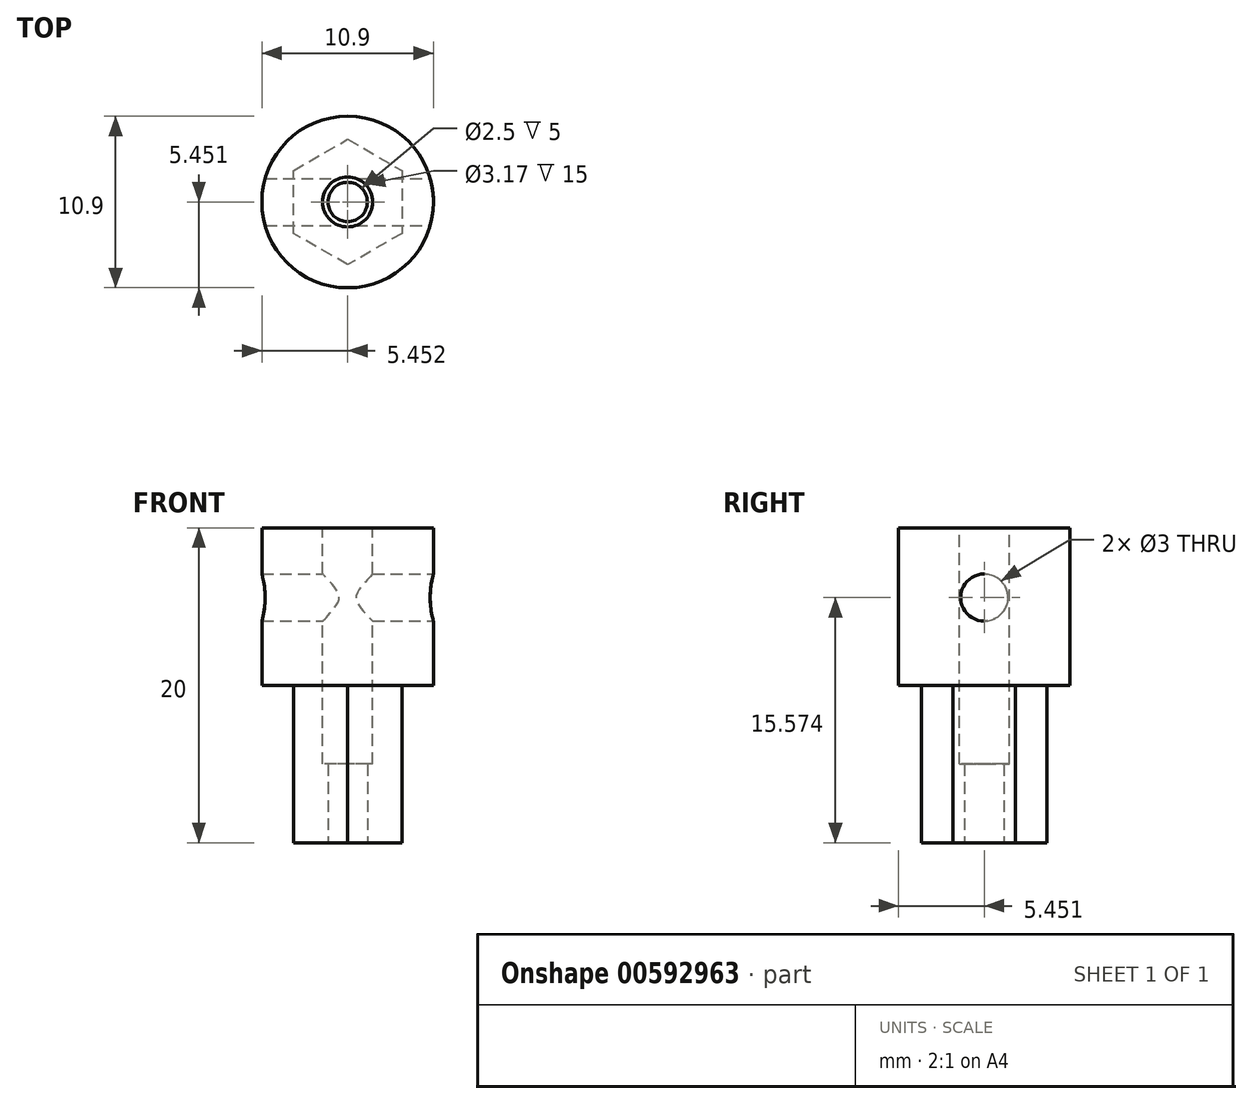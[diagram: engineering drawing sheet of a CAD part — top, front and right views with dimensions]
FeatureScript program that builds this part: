
annotation { "Feature Type Name" : "Feature", "Feature Type Description" : "" }
export const myFeature = defineFeature(function(context is Context, id is Id, definition is map)
    precondition{}
    {
        {
            var Q0;
            Q0=qCreatedBy(makeId("Top.planeOp"),FACE);
            var sketch = newSketch(context, id + "F0", { "sketchPlane" : qUnion([Q0])});
            skCircle(sketch, "E0.cCircle", {"center": v(2.23, 0.88) * mm, "radius": 3.98 * mm, "construction": true});
            skLineSegment(sketch, "E0.0", {"start": v(5.68, -1.11) * mm, "end": v(2.23, -3.1) * mm});
            skLineSegment(sketch, "E0.1", {"start": v(2.23, -3.1) * mm, "end": v(-1.22, -1.11) * mm});
            skLineSegment(sketch, "E0.2", {"start": v(-1.22, -1.11) * mm, "end": v(-1.22, 2.87) * mm});
            skLineSegment(sketch, "E0.3", {"start": v(-1.22, 2.87) * mm, "end": v(2.23, 4.86) * mm});
            skLineSegment(sketch, "E0.4", {"start": v(2.23, 4.86) * mm, "end": v(5.68, 2.87) * mm});
            skLineSegment(sketch, "E0.5", {"start": v(5.68, 2.87) * mm, "end": v(5.68, -1.11) * mm});
            skCircle(sketch, "E1", {"center": v(2.23, 0.88) * mm, "radius": 1.25 * mm});
            skSolve(sketch);
        }
        {
            var Q0;
            Q0=makeQuery(id+"F0.imprint","IMPRINT",FACE,{"disambiguationData":[TD([[makeQuery(id+"F0.imprint","IMPRINT",EDGE,{"derivedFrom":sQuery(id+"F0.wireOp",EDGE,"E0.0")}),-1.0]])]});
            extrude(context, id + "F1", {"entities" : qUnion([Q0]), "depth" : 10 * mm, "offsetDistance" : 25 * mm});
        }
        {
            var Q0;
            Q0=makeQuery(id+"F1.opExtrude","CAP_FACE",FACE,{"disambiguationData":[OSD([sQuery(id+"F0.wireOp",EDGE,"E0.0"),sQuery(id+"F0.wireOp",EDGE,"E0.1"),sQuery(id+"F0.wireOp",EDGE,"E0.2"),sQuery(id+"F0.wireOp",EDGE,"E0.3"),sQuery(id+"F0.wireOp",EDGE,"E0.4"),sQuery(id+"F0.wireOp",EDGE,"E0.5"),sQuery(id+"F0.wireOp",EDGE,"E1")])],"isStart":false});
            var sketch = newSketch(context, id + "F2", { "sketchPlane" : qUnion([Q0])});
            skCircle(sketch, "E2", {"center": v(2.23, 0.88) * mm, "radius": 5.45 * mm});
            skSolve(sketch);
        }
        {
            var Q0;
            Q0=makeQuery(id+"F2.imprint","IMPRINT",FACE,{"disambiguationData":[TD([[makeQuery(id+"F2.imprint","IMPRINT",EDGE,{"derivedFrom":sQuery(id+"F2.wireOp",EDGE,"E2")}),1.0]])]});
            var Q1;
            Q1=makeQuery(id+"F2.imprint","IMPRINT",FACE,{"disambiguationData":[TD([[makeQuery(id+"F2.imprint","IMPRINT",EDGE,{"derivedFrom":makeQuery(id+"F1.opExtrude","CAP_EDGE",EDGE,{"disambiguationData":[OSD([sQuery(id+"F0.wireOp",EDGE,"E0.0")])],"isStart":false})}),-1.0]])]});
            var Q2;
            Q2=makeQuery(id+"F2.imprint","IMPRINT",FACE,{"disambiguationData":[TD([[makeQuery(id+"F2.imprint","IMPRINT",EDGE,{"derivedFrom":makeQuery(id+"F1.opExtrude","CAP_EDGE",EDGE,{"disambiguationData":[OSD([sQuery(id+"F0.wireOp",EDGE,"E1")])],"isStart":false})}),1.0]])]});
            extrude(context, id + "F3", {"entities" : qUnion([Q0, Q1, Q2]), "operationType" : NewBodyOperationType.ADD, "depth" : 10 * mm, "offsetDistance" : 25 * mm});
        }
        {
            var Q0;
            Q0=makeQuery(id+"F3.opExtrude","CAP_FACE",FACE,{"disambiguationData":[OSD([sQuery(id+"F2.wireOp",EDGE,"E2")])],"isStart":false});
            var sketch = newSketch(context, id + "F4", { "sketchPlane" : qUnion([Q0])});
            skCircle(sketch, "E3", {"center": v(2.23, 0.88) * mm, "radius": 1.59 * mm});
            skLineSegment(sketch, "E4", {"start": v(2.23, 0.88) * mm, "end": v(7.68, 0.88) * mm, "construction": true});
            skSolve(sketch);
        }
        {
            var Q0;
            Q0=makeQuery(id+"F4.imprint","IMPRINT",FACE,{"disambiguationData":[TD([[makeQuery(id+"F4.imprint","IMPRINT",EDGE,{"derivedFrom":sQuery(id+"F4.wireOp",EDGE,"E3")}),1.0]])]});
            extrude(context, id + "F5", {"entities" : qUnion([Q0]), "operationType" : NewBodyOperationType.REMOVE, "oppositeDirection" : true, "depth" : 15 * mm, "offsetDistance" : 25 * mm});
        }
        {
            var Q0;
            Q0=makeQuery(id+"F1.opExtrude","SWEPT_FACE",FACE,{"disambiguationData":[OSD([sQuery(id+"F0.wireOp",EDGE,"E0.5")])]});
            var sketch = newSketch(context, id + "F6", { "sketchPlane" : qUnion([Q0])});
            skCircle(sketch, "E5", {"center": v(0.88, 15.57) * mm, "radius": 1.5 * mm});
            skPoint(sketch, "E5.centerSnap0", {"position": v(0.88, 10) * mm});
            skSolve(sketch);
        }
        {
            var Q0;
            Q0=makeQuery(id+"F6.imprint","IMPRINT",FACE,{"disambiguationData":[TD([[makeQuery(id+"F6.imprint","IMPRINT",EDGE,{"derivedFrom":sQuery(id+"F6.wireOp",EDGE,"E5")}),1.0]])]});
            extrude(context, id + "F7", {"entities" : qUnion([Q0]), "operationType" : NewBodyOperationType.REMOVE, "endBound" : BoundingType.SYMMETRIC, "oppositeDirection" : true, "depth" : 25 * mm, "offsetDistance" : 25 * mm});
        }
    });
